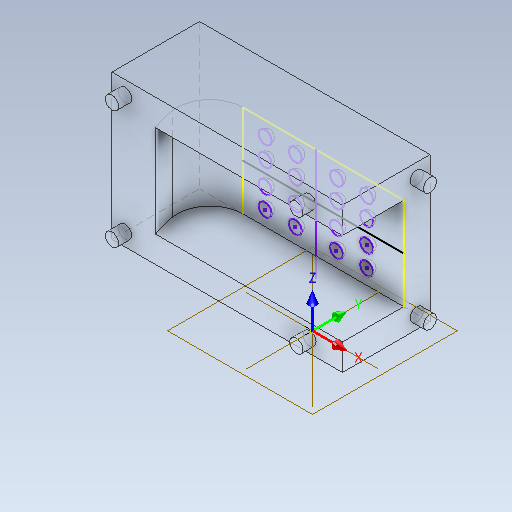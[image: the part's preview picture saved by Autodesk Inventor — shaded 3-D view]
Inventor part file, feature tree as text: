
AUTODESK INVENTOR PART (.ipt)
format: ipt  version: 2025.2 (Build 292293000, 293)  size: 553,472 bytes
history: native  units: mm
features: sketch x29, revolve x16, extrude x11, other x9, fillet x2, plane x1
ambient origin geometry x8: Origin, YZ Plane, XZ Plane, XY Plane, X Axis, Y Axis, Z Axis, Center Point
bodies: Volumenkörper2 (feature_tree), Volumenkörper3 (feature_tree)
feature tree (68):
  sketch  "Skizze1"  dims[d0=0.0mm d1=0.0mm d2=0.0mm d3=0.0mm d4=0.0mm d5=0.0mm d13=29.5mm d14=18.6mm d16=0.0mm d17=14.0mm]
  other  "BKS1"
  plane  "Arbeitsebene1"
  sketch  "Skizze5"  dims[d26=360.0deg d27=360.0deg]
  revolve  "Umdrehung2"
  revolve  "Umdrehung3"
  revolve  "Umdrehung4"
  revolve  "Umdrehung5"
  revolve  "Umdrehung6"
  revolve  "Umdrehung7"
  revolve  "Umdrehung8"
  revolve  "Umdrehung9"
  revolve  "Umdrehung10"
  revolve  "Umdrehung11"
  revolve  "Umdrehung12"
  revolve  "Umdrehung13"
  revolve  "Umdrehung14"
  revolve  "Umdrehung15"
  revolve  "Umdrehung16"
  revolve  "Umdrehung17"
  extrude  "Extrusion3"  Depth=14.0mm TaperAngle=0.0deg
  other  "Kombinieren1"
  extrude  "Extrusion9"  Depth=5.0mm
  extrude  "Extrusion10"  TaperAngle=360.0deg  [1 undecoded]
  extrude  "Extrusion11"  TaperAngle=360.0deg  [1 undecoded]
  extrude  "Extrusion12"  TaperAngle=360.0deg  [1 undecoded]
  extrude  "Extrusion13"  TaperAngle=360.0deg  [1 undecoded]
  extrude  "Extrusion14"  TaperAngle=360.0deg  [1 undecoded]
  extrude  "Extrusion15"  TaperAngle=360.0deg  [1 undecoded]
  extrude  "Extrusion16"  TaperAngle=360.0deg  [1 undecoded]
  extrude  "Extrusion17"  TaperAngle=360.0deg  [1 undecoded]
  sketch  "Skizze6"  dims[d28=360.0deg d29=360.0deg]
  sketch  "Skizze7"  dims[d30=360.0deg d31=360.0deg]
  sketch  "Skizze8"  dims[d32=360.0deg d33=360.0deg]
  sketch  "Skizze9"  dims[d34=360.0deg d35=360.0deg]
  sketch  "Skizze10"  dims[d36=360.0deg d37=360.0deg]
  sketch  "Skizze11"  dims[d38=360.0deg d39=360.0deg]
  sketch  "Skizze12"  dims[d40=360.0deg d41=360.0deg]
  sketch  "Skizze13"  dims[d42=35.0mm d43=0.0mm d52=4.0mm d53=4.0mm d54=4.0mm]
  sketch  "Skizze14"  dims[d55=4.0mm]
  sketch  "Skizze15"  dims[d62=2.0mm d63=0.0mm]
  sketch  "Skizze16"  dims[d64=2.0mm d65=0.0mm]
  sketch  "Skizze17"  dims[d66=2.0mm d67=0.0mm]
  sketch  "Skizze18"  dims[d68=2.0mm d69=0.0mm]
  sketch  "Skizze19"  dims[d70=2.0mm]
  sketch  "Skizze20"  dims[d71=2.0mm]
  sketch  "Skizze21"  dims[d73=2.0mm]
  sketch  "Skizze22"  dims[d74=2.0mm]
  sketch  "Skizze29"  dims[d76=2.0mm]
  sketch  "Skizze30"  dims[d77=2.0mm]
  sketch  "Skizze31"  dims[d80=2.0mm]
  sketch  "Skizze32"  dims[d82=2.0mm]
  sketch  "Skizze33"  dims[d83=2.0mm]
  sketch  "Skizze34"  dims[d84=2.0mm]
  sketch  "Skizze35"  dims[d85=2.0mm]
  sketch  "Skizze36"  dims[d86=2.0mm]
  sketch  "Skizze37"  dims[d87=40.0mm d88=0.0mm d90=2.0mm d91=0.0mm d92=2.0mm d93=0.0mm d94=2.0mm d95=0.0mm d96=2.0mm d97=0.0mm d98=2.0mm d99=2.0mm d100=2.0mm d101=2.0mm d102=2.0mm d103=2.0mm d104=2.0mm d105=2.0mm d106=5.0mm d107=2.0mm d108=2.0mm d109=5.0mm d111=14.0mm d114=9.3mm d115=9.3mm d110=0.5mm d112=0.5mm d113=0.872665mm]
  other  "BKS1: YZ-Ebene"
  other  "BKS1: XZ-Ebene"
  other  "BKS1: XY-Ebene"
  other  "BKS1: X-Achse"
  other  "BKS1: Y-Achse"
  other  "BKS1: Z-Achse"
  other  "BKS1: Mittelpunkt"
  sketch  "Skizze3"  dims[d18=15.0mm d19=5.0mm]
  extrude  "Extrusion2"  Depth=4.0mm
  fillet  "Rundung4"  Radius=4.0mm
  fillet  "Rundung3"  Radius=4.0mm
note: 8 required parameter values undecoded (feature->parameter linkage not recoverable at this tier; creation-order binding heuristic only, values carry confidence <= 0.55)
